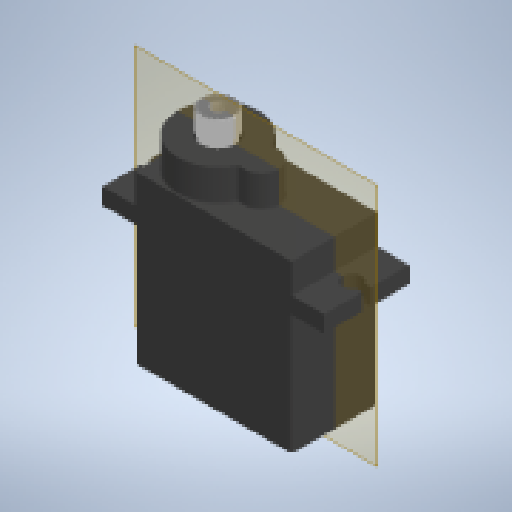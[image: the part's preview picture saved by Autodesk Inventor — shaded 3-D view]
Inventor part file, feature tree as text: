
AUTODESK INVENTOR PART (.ipt)
format: ipt  version: 2023 (Build 270158000, 158)  size: 623,616 bytes
history: native  units: in
note: dims shown in document units (in); Inventor stores cm internally (conversion verified against a paired STEP export)
features: sketch x7, extrude x5, hole x2, fillet x2, mirror x1, pattern_circular x1, chamfer x1, other x1, plane x1
ambient origin geometry x8: Origin, YZ Plane, XZ Plane, XY Plane, X Axis, Y Axis, Z Axis, Center Point
bodies: Solid1 (feature_tree), Solid2 (feature_tree)
feature tree (21):
  extrude  "Extrusion1"  Depth=0.0945in
  extrude  "Extrusion2"  Depth=0.8976in
  hole  "Hole1"  [1 undecoded]
  extrude  "Extrusion3"  Depth=0.248in
  mirror  "Mirror1"
  fillet  "Fillet1"  Radius=0.2008in
  fillet  "Fillet2"  Radius=0.0376in
  extrude  "Extrusion4"  Depth=0.1693in
  extrude  "Extrusion5"  Depth=0.0974in TaperAngle=0.0deg
  pattern_circular  "Circular Pattern1"  [2 undecoded]
  chamfer  "Chamfer2"  Distance=0.0236in
  hole  "Hole2"  [1 undecoded]
  other  "Ref Sketch"
  plane  "Work Plane2"
  sketch  "Sketch1"  dims[d5=0.185in d6=0.0945in]
  sketch  "Sketch2"  dims[d7=0.689in d8=0.8976in]
  sketch  "Sketch3"  dims[d11=0.4882in d12=0.0in d13=0.2323in]
  sketch  "Sketch4"  dims[d14=0.0984in d15=0.248in d16=0.2008in d17=0.0376in]
  sketch  "Sketch5"  dims[d18=0.1772in d19=0.0in d20=0.1693in]
  sketch  "Sketch6"  dims[d21=0.185in]
  sketch  "Sketch7"  dims[d22=0.1083in d23=0.2362in d24=0.1575in d25=0.0787in d26=90.0deg d27=0.315in d28=0.8108in d29=0.1969in d30=0.0in d31=0.0472in d34=0.0236in d35=0.0079in d36=0.0157in d39=0.1719in d41=0.1378in d42=0.3937in d43=0.0in d44=0.0in d50=0.0974in d51=0.0974in d52=0.004in d53=0.0875in d55=0.0124in d56=0.0124in d57=0.0025in d58=0.04in d59=0.0724in d60=0.0272in d61=0.0544in d62=0.04in d63=0.1181in d64=0.0in d65=7.874in d66=360.0deg d68=0.0059in d69=0.0787in d70=45.0deg d71=0.0793in d72=0.2362in d73=0.1575in d74=0.0787in d75=90.0deg d76=0.315in d77=0.8108in d78=0.6654in d79=0.2323in d80=0.2165in d81=1.1024in d86=0.0827in d87=0.8976in d88=0.4882in d89=1.2677in]
note: 4 required parameter values undecoded (feature->parameter linkage not recoverable at this tier; creation-order binding heuristic only, values carry confidence <= 0.55)
